# Revit family: Haworth_ActiveComponents_RectangularHalfConferenceEnd_Reside_BUILD
name_source: partatom
category: Furniture Systems
revit_build: Autodesk Revit Architecture 2015 (Build: 20141119_1515(x64)
units: mm (PartAtom-declared; Revit-internal decimal feet)

## types (4) — shared parameters
Actual Height = 29 3/16"
Assembly Code = E2020200
Custom Screen Size = No
Custom Size = No
Leg Finish = Haworth _ Paint _ Metallic Silver
Manufacturer = Haworth
Max Depth = 30"
Max Screen Width = 72"
Max Width = 72"
Max. Depth = 30"
Min Depth = 24"
Min Screen Width = 60"
Min Width = 60"
Min. Depth = 24"
Model = WKYB
Overhang 18in = Yes
Overhang 9in = No
Overhang Dimension = 18"
Revision Number = 1
Screen Finish = Haworth _ Fabric _ Class _ Light Cool Neutral
Screen Offset = 28 1/4"
Size = Verify Final Dim. w/ Haworth
Standard Screen Widths = 60, 72 inches
Standard Worksurface Depths = 24, 30 inches
Standard Worksurface Widths = 60, 72 inches
Support Height = 28"
Sustainability Info = http://www.haworth.com
Top Thickness = 1 3/16"
URL = www.haworth.com
URL - Product = https://www.haworth.com
Warranty = http://www.haworth.com

## per-type parameters (varying)
| type | Actual Depth | Actual Screen Width | Actual Width | Depth | Description | Overall Width | Screen Width | Width |
| 30d 72w - 18" Overhang | 30" | 72" | 72" | 30" | Haworth Reside - Worksurface - Rectangular Half Conference End - 30d 72w | 90" | 72" | 72" |
| 30d 60w - 18" Overhang | 30" | 60" | 60" | 30" | Haworth Reside - Worksurface - Rectangular Half Conference End - 30d 60w | 78" | 60" | 60" |
| 24d 72w - 18" Overhang | 24" | 72" | 72" | 24" | Haworth Reside - Worksurface - Rectangular Half Conference End - 24d 72w | 90" | 72" | 72" |
| 24d 60w - 18" Overhang | 24" | 60" | 60" | 24" | Haworth Reside - Worksurface - Rectangular Half Conference End - 24d 60w | 78" | 60" | 60" |

## geometry (parser evidence)
native form markers: Blend x82, Sweep x13
no freeform markers — native parametric forms only
